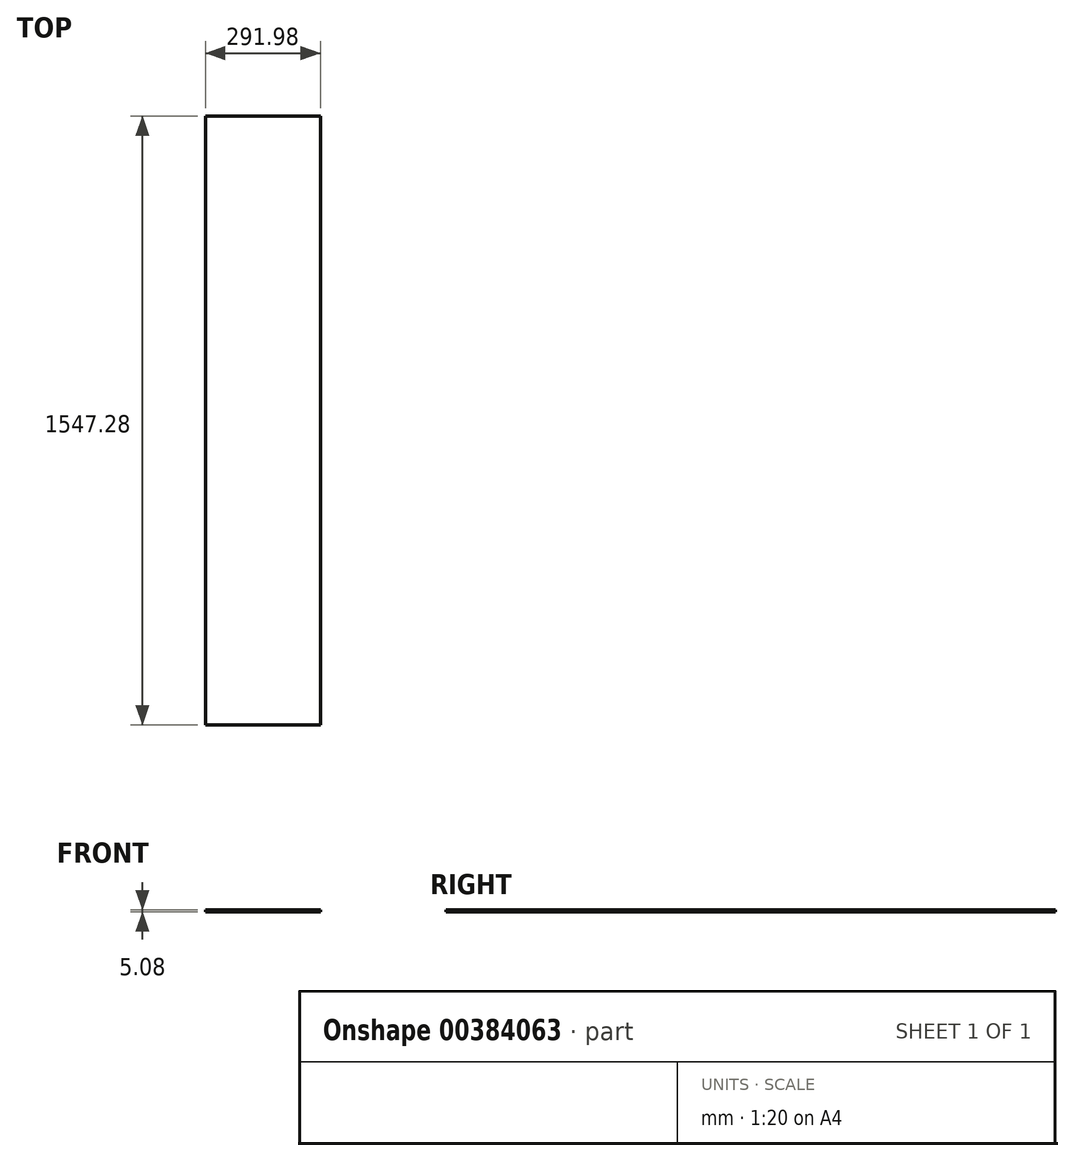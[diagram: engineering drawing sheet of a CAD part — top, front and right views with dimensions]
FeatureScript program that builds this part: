
annotation { "Feature Type Name" : "Feature", "Feature Type Description" : "" }
export const myFeature = defineFeature(function(context is Context, id is Id, definition is map)
    precondition{}
    {
        {
            var Q0;
            Q0=qCreatedBy(makeId("Top.planeOp"),FACE);
            var sketch = newSketch(context, id + "F0", { "sketchPlane" : qUnion([Q0])});
            skLineSegment(sketch, "E0.bottom", {"start": v(-146, -773.64) * mm, "end": v(146, -773.64) * mm});
            skLineSegment(sketch, "E0.top", {"start": v(-146, 773.64) * mm, "end": v(146, 773.64) * mm});
            skLineSegment(sketch, "E0.left", {"start": v(-146, -773.64) * mm, "end": v(-146, 773.64) * mm});
            skLineSegment(sketch, "E0.right", {"start": v(146, -773.64) * mm, "end": v(146, 773.64) * mm});
            skPoint(sketch, "E0.middle", {"position": v(0, 0) * mm});
            skSolve(sketch);
        }
        {
            var Q0;
            Q0=makeQuery(id+"F0.imprint","IMPRINT",FACE,{"disambiguationData":[TD([[makeQuery(id+"F0.imprint","IMPRINT",EDGE,{"derivedFrom":sQuery(id+"F0.wireOp",EDGE,"E0.bottom")}),1.0]])]});
            extrude(context, id + "F1", {"entities" : qUnion([Q0]), "depth" : 5.08 * mm});
        }
    });
